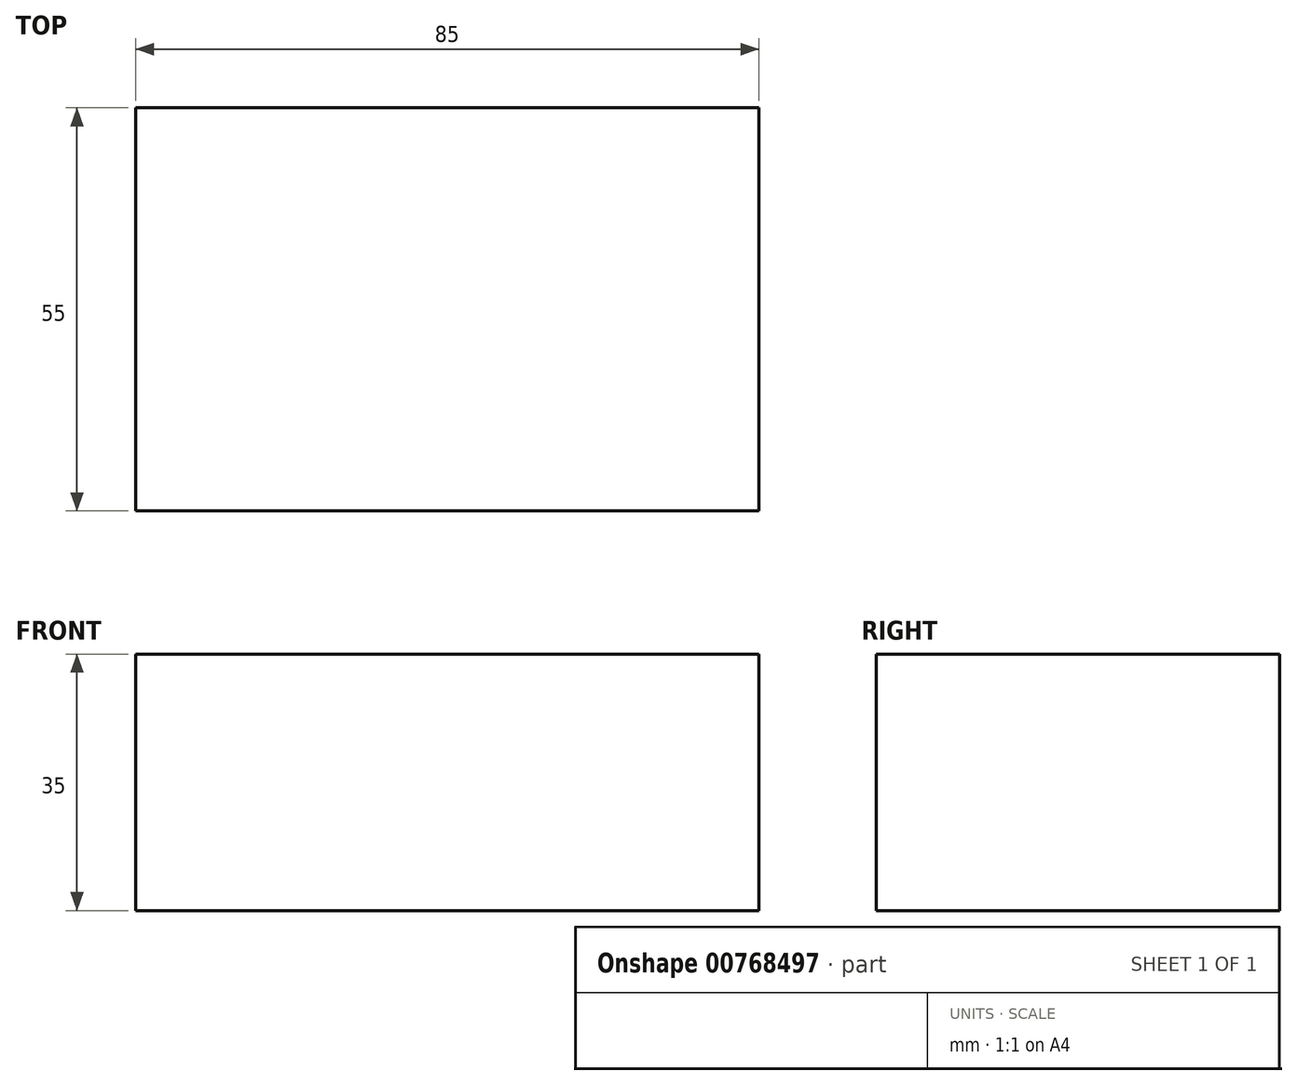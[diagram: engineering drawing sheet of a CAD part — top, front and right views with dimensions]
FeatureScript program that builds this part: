
annotation { "Feature Type Name" : "Feature", "Feature Type Description" : "" }
export const myFeature = defineFeature(function(context is Context, id is Id, definition is map)
    precondition{}
    {
        {
            var Q0;
            Q0=qCreatedBy(makeId("Top.planeOp"),FACE);
            var sketch = newSketch(context, id + "F0", { "sketchPlane" : qUnion([Q0])});
            skLineSegment(sketch, "E0.bottom", {"start": v(0, 0) * mm, "end": v(85, 0) * mm});
            skLineSegment(sketch, "E0.top", {"start": v(0, 55) * mm, "end": v(85, 55) * mm});
            skLineSegment(sketch, "E0.left", {"start": v(0, 0) * mm, "end": v(0, 55) * mm});
            skLineSegment(sketch, "E0.right", {"start": v(85, 0) * mm, "end": v(85, 55) * mm});
            skSolve(sketch);
        }
        {
            var Q0;
            Q0=makeQuery(id+"F0.imprint","IMPRINT",FACE,{"disambiguationData":[TD([[makeQuery(id+"F0.imprint","IMPRINT",EDGE,{"derivedFrom":sQuery(id+"F0.wireOp",EDGE,"E0.bottom")}),1.0]])]});
            extrude(context, id + "F1", {"entities" : qUnion([Q0]), "depth" : 35 * mm, "offsetDistance" : 25 * mm});
        }
    });
